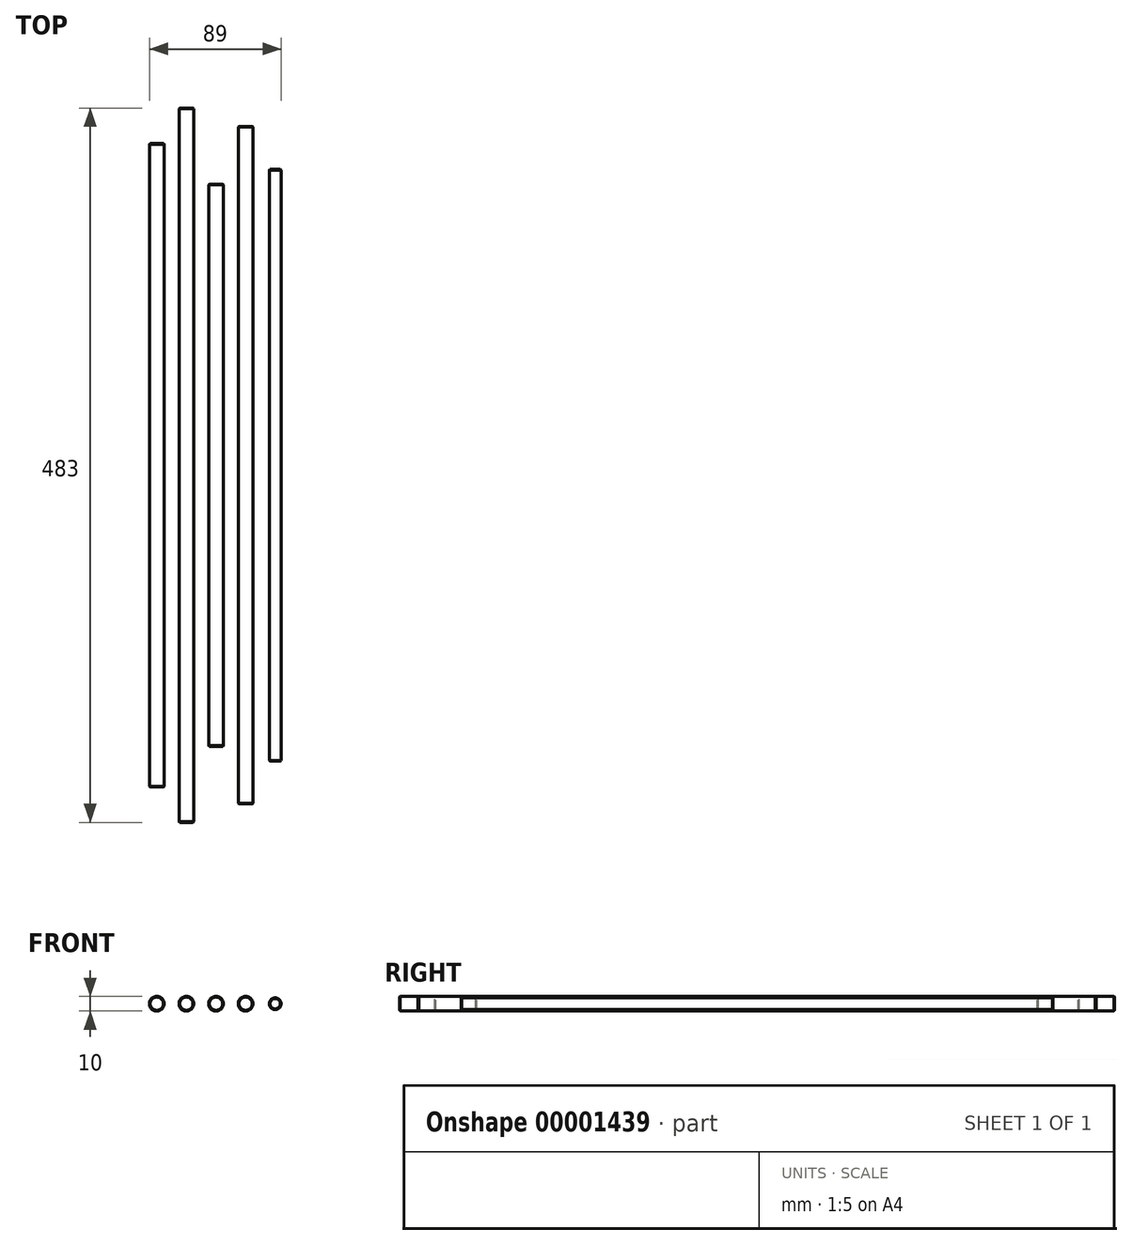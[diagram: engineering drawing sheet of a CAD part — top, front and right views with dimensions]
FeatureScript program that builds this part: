
annotation { "Feature Type Name" : "Feature", "Feature Type Description" : "" }
export const myFeature = defineFeature(function(context is Context, id is Id, definition is map)
    precondition{}
    {
        {
            var Q0;
            Q0=qCreatedBy(makeId("Front.planeOp"),FACE);
            var sketch = newSketch(context, id + "F0", { "sketchPlane" : qUnion([Q0])});
            skCircle(sketch, "E0", {"center": v(0, 0) * mm, "radius": 5 * mm});
            skSolve(sketch);
        }
        {
            var Q0;
            Q0=makeQuery(id+"F0.imprint","IMPRINT",FACE,{"disambiguationData":[TD([[makeQuery(id+"F0.imprint","IMPRINT",EDGE,{"derivedFrom":sQuery(id+"F0.wireOp",EDGE,"E0")}),1.0]])]});
            extrude(context, id + "F1", {"entities" : qUnion([Q0]), "depth" : 458 * mm, "symmetric" : true});
        }
        {
            var Q0;
            Q0=makeQuery(id+"F1.opExtrude","CAP_EDGE",EDGE,{"disambiguationData":[OSD([sQuery(id+"F0.wireOp",EDGE,"E0")])],"isStart":false});
            var Q1;
            Q1=makeQuery(id+"F1.opExtrude","CAP_EDGE",EDGE,{"disambiguationData":[OSD([sQuery(id+"F0.wireOp",EDGE,"E0")])],"isStart":true});
            chamfer(context, id + "F2", {"entities" : qUnion([Q0, Q1]), "width" : .5 * mm, "tangentPropagation" : true});
        }
        {
            var Q0;
            Q0=qCreatedBy(makeId("Front.planeOp"),FACE);
            var sketch = newSketch(context, id + "F3", { "sketchPlane" : qUnion([Q0])});
            skLineSegment(sketch, "E1", {"start": v(0, 0) * mm, "end": v(20, 0) * mm, "construction": true});
            skCircle(sketch, "E2", {"center": v(20, 0) * mm, "radius": 4 * mm});
            skSolve(sketch);
        }
        {
            var Q0;
            Q0=makeQuery(id+"F3.imprint","IMPRINT",FACE,{"disambiguationData":[TD([[makeQuery(id+"F3.imprint","IMPRINT",EDGE,{"derivedFrom":sQuery(id+"F3.wireOp",EDGE,"E2")}),1.0]])]});
            extrude(context, id + "F4", {"entities" : qUnion([Q0]), "depth" : 400 * mm, "symmetric" : true});
        }
        {
            var Q0;
            Q0=makeQuery(id+"F4.opExtrude","CAP_EDGE",EDGE,{"disambiguationData":[OSD([sQuery(id+"F3.wireOp",EDGE,"E2")])],"isStart":false});
            var Q1;
            Q1=makeQuery(id+"F4.opExtrude","CAP_EDGE",EDGE,{"disambiguationData":[OSD([sQuery(id+"F3.wireOp",EDGE,"E2")])],"isStart":true});
            chamfer(context, id + "F5", {"entities" : qUnion([Q0, Q1]), "width" : .5 * mm, "tangentPropagation" : true});
        }
        {
            var Q0;
            Q0=qCreatedBy(makeId("Front.planeOp"),FACE);
            var sketch = newSketch(context, id + "F6", { "sketchPlane" : qUnion([Q0])});
            skLineSegment(sketch, "E3", {"start": v(0, 0) * mm, "end": v(-20, 0) * mm, "construction": true});
            skCircle(sketch, "E4", {"center": v(-20, 0) * mm, "radius": 5 * mm});
            skSolve(sketch);
        }
        {
            var Q0;
            Q0=makeQuery(id+"F6.imprint","IMPRINT",FACE,{"disambiguationData":[TD([[makeQuery(id+"F6.imprint","IMPRINT",EDGE,{"derivedFrom":sQuery(id+"F6.wireOp",EDGE,"E4")}),1.0]])]});
            extrude(context, id + "F7", {"entities" : qUnion([Q0]), "depth" : 380 * mm, "symmetric" : true});
        }
        {
            var Q0;
            Q0=makeQuery(id+"F7.opExtrude","CAP_FACE",FACE,{"disambiguationData":[OSD([sQuery(id+"F6.wireOp",EDGE,"E4")])],"isStart":false});
            var Q1;
            Q1=makeQuery(id+"F7.opExtrude","CAP_FACE",FACE,{"disambiguationData":[OSD([sQuery(id+"F6.wireOp",EDGE,"E4")])],"isStart":true});
            chamfer(context, id + "F8", {"entities" : qUnion([Q0, Q1]), "width" : .5 * mm, "tangentPropagation" : true});
        }
        {
            var Q0;
            Q0=makeQuery(id+"F7.opExtrude","SWEPT_BODY",BODY,{"disambiguationData":[OSD([sQuery(id+"F6.wireOp",EDGE,"E4")])]});
            var Q1;
            Q1=makeQuery(id+"F1.opExtrude","SWEPT_BODY",BODY,{"disambiguationData":[OSD([sQuery(id+"F0.wireOp",EDGE,"E0")])]});
            var Q2;
            Q2=makeQuery(id+"F4.opExtrude","SWEPT_BODY",BODY,{"disambiguationData":[OSD([sQuery(id+"F3.wireOp",EDGE,"E2")])]});
            transform(context, id + "F9", {"entities" : qUnion([Q0, Q1, Q2]), "transformType" : TransformType.TRANSLATION_3D, "dx" : 40 * mm, "dy" : 0 * mm, "dz" : 0 * mm, "makeCopy" : false});
        }
        {
            var Q0;
            Q0=makeQuery(id+"F0.imprint","IMPRINT",FACE,{"disambiguationData":[TD([[makeQuery(id+"F0.imprint","IMPRINT",EDGE,{"derivedFrom":sQuery(id+"F0.wireOp",EDGE,"E0")}),1.0]])]});
            extrude(context, id + "F10", {"entities" : qUnion([Q0]), "depth" : 483 * mm, "symmetric" : true});
        }
        {
            var Q0;
            Q0=makeQuery(id+"F10.opExtrude","CAP_EDGE",EDGE,{"disambiguationData":[OSD([sQuery(id+"F0.wireOp",EDGE,"E0")])],"isStart":false});
            var Q1;
            Q1=makeQuery(id+"F10.opExtrude","CAP_EDGE",EDGE,{"disambiguationData":[OSD([sQuery(id+"F0.wireOp",EDGE,"E0")])],"isStart":true});
            chamfer(context, id + "F11", {"entities" : qUnion([Q0, Q1]), "width" : .5 * mm, "tangentPropagation" : true});
        }
        {
            var Q0;
            Q0=makeQuery(id+"F10.opExtrude","SWEPT_BODY",BODY,{"disambiguationData":[OSD([sQuery(id+"F0.wireOp",EDGE,"E0")])]});
            var Q1;
            Q1=makeQuery(id+"F7.opExtrude","SWEPT_BODY",BODY,{"disambiguationData":[OSD([sQuery(id+"F6.wireOp",EDGE,"E4")])]});
            var Q2;
            Q2=makeQuery(id+"F1.opExtrude","SWEPT_BODY",BODY,{"disambiguationData":[OSD([sQuery(id+"F0.wireOp",EDGE,"E0")])]});
            var Q3;
            Q3=makeQuery(id+"F4.opExtrude","SWEPT_BODY",BODY,{"disambiguationData":[OSD([sQuery(id+"F3.wireOp",EDGE,"E2")])]});
            transform(context, id + "F12", {"entities" : qUnion([Q0, Q1, Q2, Q3]), "transformType" : TransformType.TRANSLATION_3D, "dx" : 20 * mm, "dy" : 0 * mm, "dz" : 0 * mm, "makeCopy" : false});
        }
        {
            var Q0;
            Q0=makeQuery(id+"F0.imprint","IMPRINT",FACE,{"disambiguationData":[TD([[makeQuery(id+"F0.imprint","IMPRINT",EDGE,{"derivedFrom":sQuery(id+"F0.wireOp",EDGE,"E0")}),1.0]])]});
            extrude(context, id + "F13", {"entities" : qUnion([Q0]), "depth" : 435 * mm, "symmetric" : true});
        }
        {
            var Q0;
            Q0=makeQuery(id+"F13.opExtrude","CAP_EDGE",EDGE,{"disambiguationData":[OSD([sQuery(id+"F0.wireOp",EDGE,"E0")])],"isStart":false});
            var Q1;
            Q1=makeQuery(id+"F13.opExtrude","CAP_EDGE",EDGE,{"disambiguationData":[OSD([sQuery(id+"F0.wireOp",EDGE,"E0")])],"isStart":true});
            chamfer(context, id + "F14", {"entities" : qUnion([Q0, Q1]), "width" : .5 * mm, "tangentPropagation" : true});
        }
    });
